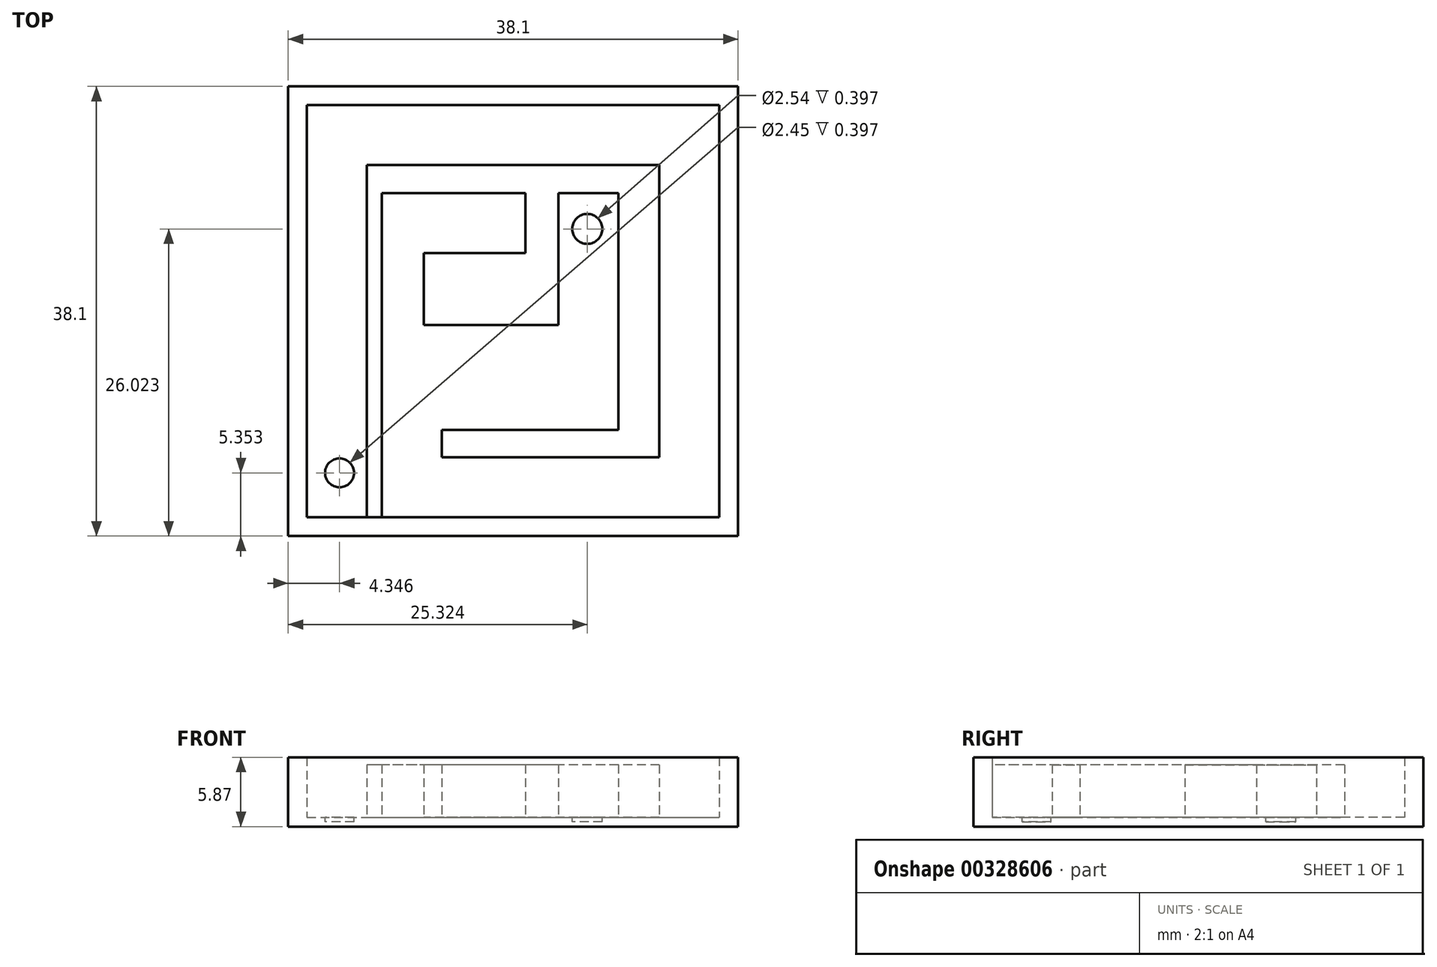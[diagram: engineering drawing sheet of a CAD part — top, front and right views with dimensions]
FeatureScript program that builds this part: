
annotation { "Feature Type Name" : "Feature", "Feature Type Description" : "" }
export const myFeature = defineFeature(function(context is Context, id is Id, definition is map)
    precondition{}
    {
        {
            var Q0;
            Q0=qCreatedBy(makeId("Top.planeOp"),FACE);
            var sketch = newSketch(context, id + "F0", { "sketchPlane" : qUnion([Q0])});
            skLineSegment(sketch, "E0.bottom", {"start": v(-16.73, 15.42) * mm, "end": v(21.37, 15.42) * mm});
            skLineSegment(sketch, "E0.top", {"start": v(-16.73, -22.68) * mm, "end": v(21.37, -22.68) * mm});
            skLineSegment(sketch, "E0.left", {"start": v(-16.73, 15.42) * mm, "end": v(-16.73, -22.68) * mm});
            skLineSegment(sketch, "E0.right", {"start": v(21.37, 15.42) * mm, "end": v(21.37, -22.68) * mm});
            skSolve(sketch);
        }
        {
            var Q0;
            Q0=makeQuery(id+"F0.imprint","IMPRINT",FACE,{"disambiguationData":[TD([[makeQuery(id+"F0.imprint","IMPRINT",EDGE,{"derivedFrom":sQuery(id+"F0.wireOp",EDGE,"E0.bottom")}),-1.0]])]});
            extrude(context, id + "F1", {"entities" : qUnion([Q0]), "depth" : 0.8 * mm});
        }
        {
            var Q0;
            Q0=makeQuery(id+"F1.opExtrude","CAP_FACE",FACE,{"disambiguationData":[OSD([sQuery(id+"F0.wireOp",EDGE,"E0.bottom"),sQuery(id+"F0.wireOp",EDGE,"E0.top"),sQuery(id+"F0.wireOp",EDGE,"E0.left"),sQuery(id+"F0.wireOp",EDGE,"E0.right")])],"isStart":false});
            var sketch = newSketch(context, id + "F2", { "sketchPlane" : qUnion([Q0])});
            skLineSegment(sketch, "E1.0", {"start": v(-15.14, 13.83) * mm, "end": v(19.78, 13.83) * mm});
            skLineSegment(sketch, "E1.1", {"start": v(-15.14, 13.83) * mm, "end": v(-15.14, -21.1) * mm});
            skLineSegment(sketch, "E1.2", {"start": v(-15.14, -21.1) * mm, "end": v(19.78, -21.1) * mm});
            skLineSegment(sketch, "E1.3", {"start": v(19.78, 13.83) * mm, "end": v(19.78, -21.1) * mm});
            skSolve(sketch);
        }
        {
            var Q0;
            Q0=makeQuery(id+"F2.imprint","IMPRINT",FACE,{"disambiguationData":[TD([[makeQuery(id+"F2.imprint","IMPRINT",EDGE,{"derivedFrom":sQuery(id+"F2.wireOp",EDGE,"E1.0")}),1.0]])]});
            extrude(context, id + "F3", {"entities" : qUnion([Q0]), "operationType" : NewBodyOperationType.ADD, "depth" : 5.08 * mm});
        }
        {
            var Q0;
            Q0=makeQuery(id+"F1.opExtrude","CAP_FACE",FACE,{"disambiguationData":[OSD([sQuery(id+"F0.wireOp",EDGE,"E0.bottom"),sQuery(id+"F0.wireOp",EDGE,"E0.top"),sQuery(id+"F0.wireOp",EDGE,"E0.left"),sQuery(id+"F0.wireOp",EDGE,"E0.right")])],"isStart":false});
            var sketch = newSketch(context, id + "F4", { "sketchPlane" : qUnion([Q0])});
            skLineSegment(sketch, "E2.bottom", {"start": v(-10.06, -21.1) * mm, "end": v(-8.8, -21.1) * mm});
            skLineSegment(sketch, "E2.top", {"start": v(-10.06, 8.75) * mm, "end": v(-8.8, 8.75) * mm});
            skLineSegment(sketch, "E2.left", {"start": v(-10.06, -21.1) * mm, "end": v(-10.06, 8.75) * mm});
            skLineSegment(sketch, "E2.right", {"start": v(-8.8, -21.1) * mm, "end": v(-8.8, 6.36) * mm});
            skLineSegment(sketch, "E3.bottom", {"start": v(-8.8, 8.75) * mm, "end": v(14.7, 8.75) * mm});
            skLineSegment(sketch, "E3.top", {"start": v(-8.8, 6.36) * mm, "end": v(3.37, 6.36) * mm});
            skLineSegment(sketch, "E3.right", {"start": v(14.7, 8.75) * mm, "end": v(14.7, 6.36) * mm});
            skLineSegment(sketch, "E4.bottom", {"start": v(2.32, -21.1) * mm, "end": v(11.23, -21.1) * mm});
            skLineSegment(sketch, "E4.top", {"start": v(2.32, -9.87) * mm, "end": v(11.23, -9.87) * mm});
            skLineSegment(sketch, "E4.left", {"start": v(2.32, -21.1) * mm, "end": v(2.32, -12.04) * mm});
            skLineSegment(sketch, "E4.right", {"start": v(11.23, -21.1) * mm, "end": v(11.23, -9.87) * mm});
            skLineSegment(sketch, "E5.bottom", {"start": v(2.32, -9.87) * mm, "end": v(-1.71, -9.87) * mm});
            skLineSegment(sketch, "E5.top", {"start": v(2.32, -12.04) * mm, "end": v(-3.71, -12.04) * mm});
            skLineSegment(sketch, "E5.left", {"start": v(2.32, -9.87) * mm, "end": v(2.32, -12.04) * mm});
            skLineSegment(sketch, "E5.right", {"start": v(-3.71, -9.87) * mm, "end": v(-3.71, -12.04) * mm});
            skLineSegment(sketch, "E6.top", {"start": v(-3.71, 1.28) * mm, "end": v(-1.71, 1.28) * mm});
            skLineSegment(sketch, "E6.left", {"start": v(-3.71, -9.87) * mm, "end": v(-3.71, 1.28) * mm});
            skLineSegment(sketch, "E6.right", {"start": v(-1.71, -9.87) * mm, "end": v(-1.71, 1.28) * mm});
            skLineSegment(sketch, "E7.left", {"start": v(14.7, 6.36) * mm, "end": v(14.7, -1.49) * mm});
            skLineSegment(sketch, "E8.top", {"start": v(3.37, -4.79) * mm, "end": v(6.15, -4.79) * mm});
            skLineSegment(sketch, "E8.left", {"start": v(3.37, 6.36) * mm, "end": v(3.37, -4.79) * mm});
            skLineSegment(sketch, "E8.right", {"start": v(6.15, 6.36) * mm, "end": v(6.15, -4.79) * mm});
            skLineSegment(sketch, "E9.bottom", {"start": v(12.77, -1.49) * mm, "end": v(11.23, -1.49) * mm});
            skLineSegment(sketch, "E9.top", {"start": v(14.7, -4.18) * mm, "end": v(11.23, -4.18) * mm});
            skLineSegment(sketch, "E9.right", {"start": v(11.23, -1.49) * mm, "end": v(11.23, -4.18) * mm});
            skLineSegment(sketch, "E10.bottom", {"start": v(19.78, -12.04) * mm, "end": v(16.31, -12.04) * mm});
            skLineSegment(sketch, "E10.top", {"start": v(19.78, -14.27) * mm, "end": v(16.31, -14.27) * mm});
            skLineSegment(sketch, "E10.left", {"start": v(19.78, -12.04) * mm, "end": v(19.78, -14.27) * mm});
            skLineSegment(sketch, "E10.right", {"start": v(16.31, -12.04) * mm, "end": v(16.31, -14.27) * mm});
            skLineSegment(sketch, "E11.trimOffspring", {"start": v(6.15, 6.36) * mm, "end": v(14.7, 6.36) * mm});
            skLineSegment(sketch, "E12", {"start": v(14.7, -1.49) * mm, "end": v(14.7, -4.18) * mm});
            skLineSegment(sketch, "E13", {"start": v(12.77, 6.36) * mm, "end": v(12.77, -1.49) * mm});
            skSolve(sketch);
        }
        {
            var Q0;
            Q0=makeQuery(id+"F4.imprint","IMPRINT",FACE,{"disambiguationData":[TD([[makeQuery(id+"F4.imprint","IMPRINT",EDGE,{"derivedFrom":sQuery(id+"F4.wireOp",EDGE,"E2.bottom")}),1.0]])]});
            var sketch = newSketch(context, id + "F5", { "sketchPlane" : qUnion([Q0])});
            skSolve(sketch);
        }
        {
            var Q0;
            Q0 = qSketchRegion(id + "F5", true);
            var Q1;
            Q1=makeQuery(id+"F4.imprint","IMPRINT",FACE,{"disambiguationData":[TD([[makeQuery(id+"F4.imprint","IMPRINT",EDGE,{"derivedFrom":sQuery(id+"F4.wireOp",EDGE,"E2.bottom")}),1.0]])]});
            extrude(context, id + "F6", {"entities" : qUnion([Q0, Q1]), "operationType" : NewBodyOperationType.ADD, "depth" : 1.59 * mm});
        }
        {
            var Q0;
            Q0=makeQuery(id+"F1.opExtrude","CAP_FACE",FACE,{"disambiguationData":[OSD([sQuery(id+"F0.wireOp",EDGE,"E0.bottom"),sQuery(id+"F0.wireOp",EDGE,"E0.top"),sQuery(id+"F0.wireOp",EDGE,"E0.left"),sQuery(id+"F0.wireOp",EDGE,"E0.right")])],"isStart":false});
            var sketch = newSketch(context, id + "F7", { "sketchPlane" : qUnion([Q0])});
            skLineSegment(sketch, "E14.bottom", {"start": v(14.7, 6.36) * mm, "end": v(11.23, 6.36) * mm});
            skLineSegment(sketch, "E14.top", {"start": v(14.7, -16.02) * mm, "end": v(11.23, -16.02) * mm});
            skLineSegment(sketch, "E14.left", {"start": v(14.7, 6.36) * mm, "end": v(14.7, -16.02) * mm});
            skLineSegment(sketch, "E14.right", {"start": v(11.23, 6.36) * mm, "end": v(11.23, -16.02) * mm});
            skLineSegment(sketch, "E15.bottom", {"start": v(3.37, 1.28) * mm, "end": v(-5.25, 1.28) * mm});
            skLineSegment(sketch, "E15.top", {"start": v(3.37, -4.79) * mm, "end": v(-5.25, -4.79) * mm});
            skLineSegment(sketch, "E15.left", {"start": v(3.37, 1.28) * mm, "end": v(3.37, -4.79) * mm});
            skLineSegment(sketch, "E15.right", {"start": v(-5.25, 1.28) * mm, "end": v(-5.25, -4.79) * mm});
            skLineSegment(sketch, "E16.bottom", {"start": v(11.23, -16.02) * mm, "end": v(-3.71, -16.02) * mm});
            skLineSegment(sketch, "E16.top", {"start": v(11.23, -13.68) * mm, "end": v(-3.71, -13.68) * mm});
            skLineSegment(sketch, "E16.left", {"start": v(11.23, -16.02) * mm, "end": v(11.23, -13.68) * mm});
            skLineSegment(sketch, "E16.right", {"start": v(-3.71, -16.02) * mm, "end": v(-3.71, -13.68) * mm});
            skLineSegment(sketch, "E17.bottom", {"start": v(-3.71, -13.68) * mm, "end": v(-1.7, -13.68) * mm});
            skLineSegment(sketch, "E17.top", {"start": v(-3.71, -9.87) * mm, "end": v(-1.7, -9.87) * mm});
            skLineSegment(sketch, "E17.left", {"start": v(-3.71, -13.68) * mm, "end": v(-3.71, -9.87) * mm});
            skLineSegment(sketch, "E17.right", {"start": v(-1.7, -13.68) * mm, "end": v(-1.7, -9.87) * mm});
            skPoint(sketch, "E18.firstSnap0", {"position": v(3.76, -13.68) * mm});
            skLineSegment(sketch, "E18.bottom", {"start": v(3.37, -13.68) * mm, "end": v(1, -13.68) * mm});
            skLineSegment(sketch, "E18.top", {"start": v(3.37, -9.87) * mm, "end": v(1, -9.87) * mm});
            skLineSegment(sketch, "E18.left", {"start": v(3.37, -13.68) * mm, "end": v(3.37, -9.87) * mm});
            skLineSegment(sketch, "E18.right", {"start": v(1, -13.68) * mm, "end": v(1, -9.87) * mm});
            skSolve(sketch);
        }
        {
            var Q0;
            Q0=makeQuery(id+"F7.imprint","IMPRINT",FACE,{"disambiguationData":[TD([[makeQuery(id+"F7.imprint","IMPRINT",EDGE,{"derivedFrom":sQuery(id+"F7.wireOp",EDGE,"E15.bottom")}),1.0]])]});
            var Q1;
            Q1=makeQuery(id+"F7.imprint","IMPRINT",FACE,{"disambiguationData":[TD([[makeQuery(id+"F7.imprint","IMPRINT",EDGE,{"derivedFrom":sQuery(id+"F7.wireOp",EDGE,"E14.bottom")}),-1.0]])]});
            var Q2;
            Q2=makeQuery(id+"F6.opExtrude","CAP_FACE",FACE,{"disambiguationData":[OSD([sQuery(id+"F4.wireOp",EDGE,"E2.bottom"),sQuery(id+"F4.wireOp",EDGE,"E2.top"),sQuery(id+"F4.wireOp",EDGE,"E2.left"),sQuery(id+"F4.wireOp",EDGE,"E2.right"),sQuery(id+"F4.wireOp",EDGE,"E3.bottom"),sQuery(id+"F4.wireOp",EDGE,"E3.top"),sQuery(id+"F4.wireOp",EDGE,"E3.right"),sQuery(id+"F4.wireOp",EDGE,"E8.top"),sQuery(id+"F4.wireOp",EDGE,"E8.left"),sQuery(id+"F4.wireOp",EDGE,"E8.right"),sQuery(id+"F4.wireOp",EDGE,"E11.trimOffspring")])],"isStart":false});
            var Q3;
            Q3=makeQuery(id+"F7.imprint","IMPRINT",FACE,{"disambiguationData":[TD([[makeQuery(id+"F7.imprint","IMPRINT",EDGE,{"derivedFrom":sQuery(id+"F7.wireOp",EDGE,"E16.bottom")}),-1.0]])]});
            var Q4;
            Q4=makeQuery(id+"F7.imprint","IMPRINT",FACE,{"disambiguationData":[TD([[makeQuery(id+"F7.imprint","IMPRINT",EDGE,{"derivedFrom":sQuery(id+"F7.wireOp",EDGE,"E18.bottom")}),-1.0]])]});
            var Q5;
            Q5=makeQuery(id+"F7.imprint","IMPRINT",FACE,{"disambiguationData":[TD([[makeQuery(id+"F7.imprint","IMPRINT",EDGE,{"derivedFrom":sQuery(id+"F7.wireOp",EDGE,"E17.bottom")}),1.0]])]});
            extrude(context, id + "F8", {"entities" : qUnion([Q0, Q1, Q2, Q3, Q4, Q5]), "operationType" : NewBodyOperationType.ADD, "depth" : 4.44 * mm});
        }
        {
            var Q0;
            Q0=makeQuery(id+"F1.opExtrude","CAP_FACE",FACE,{"disambiguationData":[OSD([sQuery(id+"F0.wireOp",EDGE,"E0.bottom"),sQuery(id+"F0.wireOp",EDGE,"E0.top"),sQuery(id+"F0.wireOp",EDGE,"E0.left"),sQuery(id+"F0.wireOp",EDGE,"E0.right")])],"isStart":false});
            var sketch = newSketch(context, id + "F9", { "sketchPlane" : qUnion([Q0])});
            skCircle(sketch, "E19", {"center": v(-12.38, -17.33) * mm, "radius": 1.22 * mm});
            skCircle(sketch, "E20", {"center": v(8.6, 3.34) * mm, "radius": 1.27 * mm});
            skSolve(sketch);
        }
        {
            var Q0;
            Q0=makeQuery(id+"F9.imprint","IMPRINT",FACE,{"disambiguationData":[TD([[makeQuery(id+"F9.imprint","IMPRINT",EDGE,{"derivedFrom":sQuery(id+"F9.wireOp",EDGE,"E19")}),1.0]])]});
            var Q1;
            Q1=makeQuery(id+"F9.imprint","IMPRINT",FACE,{"disambiguationData":[TD([[makeQuery(id+"F9.imprint","IMPRINT",EDGE,{"derivedFrom":sQuery(id+"F9.wireOp",EDGE,"E20")}),1.0]])]});
            extrude(context, id + "F10", {"entities" : qUnion([Q0, Q1]), "operationType" : NewBodyOperationType.REMOVE, "oppositeDirection" : true, "depth" : 0.4 * mm});
        }
        {
            var Q0;
            Q0=makeQuery(id+"F8.opExtrude","CAP_FACE",FACE,{"disambiguationData":[OSD([sQuery(id+"F4.wireOp",EDGE,"E2.bottom"),sQuery(id+"F4.wireOp",EDGE,"E2.top"),sQuery(id+"F4.wireOp",EDGE,"E2.left"),sQuery(id+"F4.wireOp",EDGE,"E2.right"),sQuery(id+"F4.wireOp",EDGE,"E3.bottom"),sQuery(id+"F4.wireOp",EDGE,"E3.top"),sQuery(id+"F4.wireOp",EDGE,"E3.right"),sQuery(id+"F4.wireOp",EDGE,"E8.top"),sQuery(id+"F4.wireOp",EDGE,"E8.left"),sQuery(id+"F4.wireOp",EDGE,"E8.right"),sQuery(id+"F4.wireOp",EDGE,"E11.trimOffspring")])],"isStart":false});
            extrude(context, id + "F11", {"entities" : qUnion([Q0]), "operationType" : NewBodyOperationType.ADD, "depth" : 0.23 * mm});
        }
        {
            var Q0;
            Q0=makeQuery(id+"F11.opExtrude","CAP_FACE",FACE,{"disambiguationData":[OSD([sQuery(id+"F4.wireOp",EDGE,"E2.bottom"),sQuery(id+"F4.wireOp",EDGE,"E2.top"),sQuery(id+"F4.wireOp",EDGE,"E2.left"),sQuery(id+"F4.wireOp",EDGE,"E2.right"),sQuery(id+"F4.wireOp",EDGE,"E3.bottom"),sQuery(id+"F4.wireOp",EDGE,"E3.top"),sQuery(id+"F4.wireOp",EDGE,"E3.right"),sQuery(id+"F4.wireOp",EDGE,"E8.top"),sQuery(id+"F4.wireOp",EDGE,"E8.left"),sQuery(id+"F4.wireOp",EDGE,"E8.right"),sQuery(id+"F4.wireOp",EDGE,"E11.trimOffspring")])],"isStart":false});
            var Q1;
            Q1=makeQuery(id+"F8.opExtrude","CAP_FACE",FACE,{"disambiguationData":[OSD([sQuery(id+"F7.wireOp",EDGE,"E14.bottom"),sQuery(id+"F7.wireOp",EDGE,"E14.top"),sQuery(id+"F7.wireOp",EDGE,"E14.left"),sQuery(id+"F7.wireOp",EDGE,"E14.right"),sQuery(id+"F7.wireOp",EDGE,"E16.bottom"),sQuery(id+"F7.wireOp",EDGE,"E16.top"),sQuery(id+"F7.wireOp",EDGE,"E16.right"),sQuery(id+"F7.wireOp",EDGE,"E17.top"),sQuery(id+"F7.wireOp",EDGE,"E17.left"),sQuery(id+"F7.wireOp",EDGE,"E17.right"),sQuery(id+"F7.wireOp",EDGE,"E18.top"),sQuery(id+"F7.wireOp",EDGE,"E18.left"),sQuery(id+"F7.wireOp",EDGE,"E18.right")])],"isStart":false});
            extrude(context, id + "F12", {"entities" : qUnion([Q0]), "operationType" : NewBodyOperationType.REMOVE, "endBound" : BoundingType.UP_TO_SURFACE, "oppositeDirection" : true, "endBoundEntityFace" : qUnion([Q1]), "depth" : 25.4 * mm});
        }
    });
